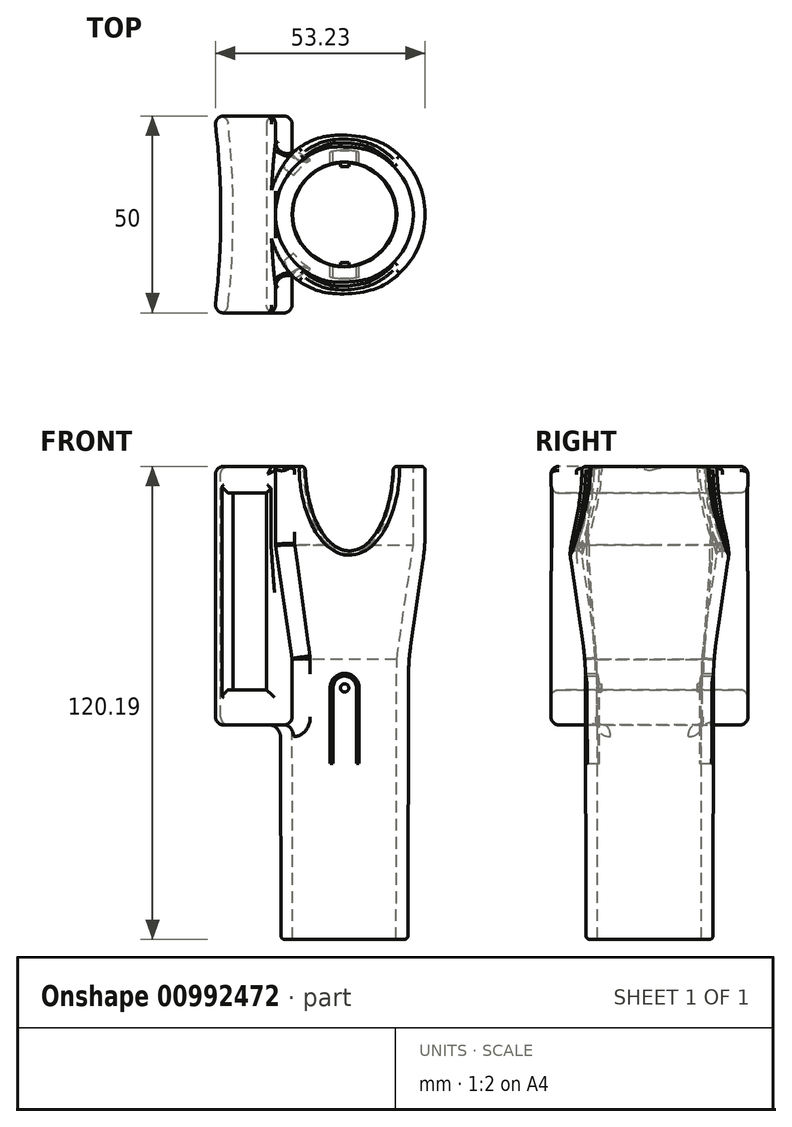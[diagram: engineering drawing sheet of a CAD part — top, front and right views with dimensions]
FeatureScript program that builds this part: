
annotation { "Feature Type Name" : "Feature", "Feature Type Description" : "" }
export const myFeature = defineFeature(function(context is Context, id is Id, definition is map)
    precondition{}
    {
        {
            var Q0;
            Q0=qCreatedBy(makeId("Front.planeOp"),FACE);
            var sketch = newSketch(context, id + "F0", { "sketchPlane" : qUnion([Q0])});
            skLineSegment(sketch, "E0", {"start": v(-0.06, 65.68) * mm, "end": v(-0.06, -68.18) * mm, "construction": true});
            skLineSegment(sketch, "E1", {"start": v(-17.56, 65.68) * mm, "end": v(-17.56, 45.68) * mm});
            skLineSegment(sketch, "E2", {"start": v(-17.56, 45.68) * mm, "end": v(-13.36, 16.68) * mm});
            skLineSegment(sketch, "E3", {"start": v(-13.36, 16.68) * mm, "end": v(-13.2, -54.45) * mm});
            skLineSegment(sketch, "E4.0", {"start": v(-16.36, 16.46) * mm, "end": v(-16.2, -54.54) * mm});
            skLineSegment(sketch, "E4.1", {"start": v(-20.56, 45.46) * mm, "end": v(-16.36, 16.46) * mm});
            skLineSegment(sketch, "E4.2", {"start": v(-20.56, 65.68) * mm, "end": v(-20.56, 45.46) * mm});
            skLineSegment(sketch, "E5", {"start": v(-20.56, 65.68) * mm, "end": v(-17.56, 65.68) * mm});
            skLineSegment(sketch, "E6", {"start": v(-16.2, -54.54) * mm, "end": v(-13.2, -54.45) * mm});
            skLineSegment(sketch, "E7", {"start": v(-20.56, 58.97) * mm, "end": v(-20.56, 45.46) * mm});
            skSolve(sketch);
        }
        {
            var Q0;
            Q0=makeQuery(id+"F0.imprint","IMPRINT",FACE,{"disambiguationData":[TD([[makeQuery(id+"F0.imprint","IMPRINT",EDGE,{"derivedFrom":sQuery(id+"F0.wireOp",EDGE,"E1")}),-1.0]])]});
            var Q1;
            Q1=sQuery(id+"F0.wireOp",EDGE,"E0");
            revolve(context, id + "F1", {"surfaceOperationType" : NewSurfaceOperationType.NEW, "entities" : qUnion([Q0]), "axis" : qUnion([Q1]), "revolveType" : RevolveType.FULL});
        }
        {
            var Q0;
            Q0=makeQuery(id+"F1.opRevolve","SWEPT_EDGE",EDGE,{"disambiguationData":[OSD([sQuery(id+"F0.wireOp",EDGE,"E4.2"),sQuery(id+"F0.wireOp",EDGE,"E5")])]});
            var Q1;
            Q1=makeQuery(id+"F1.opRevolve","SWEPT_EDGE",EDGE,{"disambiguationData":[OSD([sQuery(id+"F0.wireOp",EDGE,"E4.0"),sQuery(id+"F0.wireOp",EDGE,"E6")])]});
            var Q2;
            Q2=makeQuery(id+"F1.opRevolve","SWEPT_EDGE",EDGE,{"disambiguationData":[OSD([sQuery(id+"F0.wireOp",EDGE,"E1"),sQuery(id+"F0.wireOp",EDGE,"E5")])]});
            fillet(context, id + "F2", {"entities" : qUnion([Q0, Q1, Q2]), "radius" : 1 * mm, "tangentPropagation" : true, "allowEdgeOverflow" : false});
        }
        {
            var Q0;
            Q0=makeQuery(id+"F1.opRevolve","SWEPT_EDGE",EDGE,{"disambiguationData":[OSD([sQuery(id+"F0.wireOp",EDGE,"E4.1"),sQuery(id+"F0.wireOp",EDGE,"E7")])]});
            var Q1;
            Q1=makeQuery(id+"F1.opRevolve","SWEPT_EDGE",EDGE,{"disambiguationData":[OSD([sQuery(id+"F0.wireOp",EDGE,"E4.1"),sQuery(id+"F0.wireOp",EDGE,"WHEgpJMP-5o6V-psrv-Qzt2-RURnIkNBwz3v")])]});
            fillet(context, id + "F3", {"entities" : qUnion([Q0, Q1]), "radius" : 50 * mm, "tangentPropagation" : true, "allowEdgeOverflow" : false});
        }
        {
            var Q0;
            Q0=qCreatedBy(makeId("Front.planeOp"),FACE);
            var sketch = newSketch(context, id + "F4", { "sketchPlane" : qUnion([Q0])});
            skLineSegment(sketch, "E8", {"start": v(-17.56, 65.68) * mm, "end": v(-17.56, 45.68) * mm});
            skLineSegment(sketch, "E9", {"start": v(-13.36, 0) * mm, "end": v(-33.36, 0) * mm});
            skLineSegment(sketch, "E10", {"start": v(-33.36, 0) * mm, "end": v(-33.36, 65.68) * mm});
            skLineSegment(sketch, "E11", {"start": v(-33.36, 65.68) * mm, "end": v(-17.56, 65.68) * mm});
            skLineSegment(sketch, "E12", {"start": v(-13.36, 16.68) * mm, "end": v(-13.36, 0) * mm});
            skLineSegment(sketch, "E13", {"start": v(-17.56, 45.68) * mm, "end": v(-13.36, 16.68) * mm});
            skSolve(sketch);
        }
        {
            var Q0;
            Q0=makeQuery(id+"F4.imprint","IMPRINT",FACE,{"disambiguationData":[TD([[makeQuery(id+"F4.imprint","IMPRINT",EDGE,{"derivedFrom":sQuery(id+"F4.wireOp",EDGE,"E8")}),-1.0]])]});
            extrude(context, id + "F5", {"entities" : qUnion([Q0]), "operationType" : NewBodyOperationType.ADD, "endBound" : BoundingType.SYMMETRIC, "depth" : 50 * mm, "offsetDistance" : 25 * mm});
        }
        {
            var Q0;
            Q0=qCreatedBy(makeId("Front.planeOp"),FACE);
            var sketch = newSketch(context, id + "F6", { "sketchPlane" : qUnion([Q0])});
            skLineSegment(sketch, "E14", {"start": v(-24.08, 72.46) * mm, "end": v(-24.08, -4.6) * mm, "construction": true});
            skLineSegment(sketch, "E15.bottom", {"start": v(-19.83, 8.93) * mm, "end": v(-28.33, 8.93) * mm});
            skLineSegment(sketch, "E15.top", {"start": v(-19.83, 58.93) * mm, "end": v(-28.33, 58.93) * mm});
            skLineSegment(sketch, "E15.left", {"start": v(-19.83, 8.93) * mm, "end": v(-19.83, 58.93) * mm});
            skLineSegment(sketch, "E15.right", {"start": v(-28.33, 8.93) * mm, "end": v(-28.33, 58.93) * mm});
            skSolve(sketch);
        }
        {
            var Q0;
            Q0 = qSketchRegion(id + "F8", true);
            var Q1;
            Q1 = qSketchRegion(id + "F6", true);
            extrude(context, id + "F7", {"entities" : qUnion([Q0, Q1]), "operationType" : NewBodyOperationType.REMOVE, "endBound" : BoundingType.THROUGH_ALL, "oppositeDirection" : true, "depth" : 55 * mm, "offsetDistance" : 25 * mm, "hasSecondDirection" : true, "secondDirectionBound" : SecondDirectionBoundingType.THROUGH_ALL, "secondDirectionOppositeDirection" : false, "secondDirectionDepth" : 25 * mm});
        }
        {
            var Q0;
            Q0=makeQuery(id+"F5.opExtrude","SWEPT_FACE",FACE,{"disambiguationData":[OSD([sQuery(id+"F4.wireOp",EDGE,"E11")])]});
            var sketch = newSketch(context, id + "F8", { "sketchPlane" : qUnion([Q0])});
            skCircle(sketch, "E16", {"center": v(-235.26, 0) * mm, "radius": 211.06 * mm});
            skPoint(sketch, "E17", {"position": v(-33.36, 0) * mm});
            skSolve(sketch);
        }
        {
            var Q0;
            Q0 = qSketchRegion(id + "F6", true);
            var Q1;
            Q1=sQuery(id+"F8.wireOp",EDGE,"E16");
            sweep(context, id + "F9", {"operationType" : NewBodyOperationType.REMOVE, "profiles" : qUnion([Q0]), "path" : qUnion([Q1])});
        }
        {
            var Q0;
            {var subQ1=sQuery(id+"F4.wireOp",EDGE,"E11");var subQ6=makeQuery(id+"F5.opExtrude","SWEPT_EDGE",EDGE,{"disambiguationData":[OSD([sQuery(id+"F4.wireOp",EDGE,"E10"),subQ1])]});Q0=makeQuery(id+"F8.imprint","IMPRINT",FACE,{"disambiguationData":[TD([[makeQuery(id+"F8.imprint","IMPRINT",EDGE,{"derivedFrom":subQ6}),1.0]])]});}
            var sketch = newSketch(context, id + "F10", { "sketchPlane" : qUnion([Q0])});
            skCircle(sketch, "E18.0", {"center": v(-235.26, 0) * mm, "radius": 203.76 * mm});
            skSolve(sketch);
        }
        {
            var Q0;
            {var subQ1=sQuery(id+"F4.wireOp",EDGE,"E11");var subQ3=makeQuery(id+"F5.opExtrude","SWEPT_EDGE",EDGE,{"disambiguationData":[OSD([sQuery(id+"F4.wireOp",EDGE,"E10"),subQ1])]});var subQ10=makeQuery(id+"F8.imprint","IMPRINT",EDGE,{"derivedFrom":subQ3});Q0=makeQuery(id+"F10.imprint","IMPRINT",FACE,{"disambiguationData":[TD([[makeQuery(id+"F10.imprint","IMPRINT",EDGE,{"derivedFrom":subQ10}),-1.0]])]});}
            var Q1;
            Q1=sQuery(id+"F10.wireOp",EDGE,"E18.0");
            extrude(context, id + "F11", {"entities" : qUnion([Q0]), "operationType" : NewBodyOperationType.REMOVE, "surfaceEntities" : qUnion([Q1]), "endBound" : BoundingType.THROUGH_ALL, "oppositeDirection" : true, "depth" : 25 * mm, "offsetDistance" : 25 * mm});
        }
        {
            var Q0;
            Q0=makeQuery(id+"F11.boolean.opBoolean","COPY",EDGE,{"derivedFrom":makeQuery(id+"F11.opExtrude","CAP_EDGE",EDGE,{"disambiguationData":[OSD([sQuery(id+"F10.wireOp",EDGE,"E18.0")])],"isStart":true})});
            var Q1;
            Q1=makeQuery(id+"F5.opExtrude","CAP_EDGE",EDGE,{"disambiguationData":[OSD([sQuery(id+"F4.wireOp",EDGE,"E11")])],"isStart":false});
            var Q2;
            {var subQ0=sQuery(id+"F10.wireOp",EDGE,"E18.0");var subQ1=sQuery(id+"F4.wireOp",EDGE,"E11");var subQ2=makeQuery(id+"F5.opExtrude","CAP_EDGE",EDGE,{"disambiguationData":[OSD([subQ1])],"isStart":false});Q2=makeQuery(id+"F11.boolean.opBoolean","COPY",EDGE,{"derivedFrom":makeQuery(id+"F11.opExtrude","SWEPT_EDGE",EDGE,{"disambiguationData":[OSD([subQ1,subQ0]),TDD([makeQuery(id+"F10.imprint","INTERSECT",VERTEX,{"derivedFrom":[makeQuery(id+"F8.imprint","IMPRINT",EDGE,{"disambiguationData":[TD([[makeQuery(id+"F8.imprint","INTERSECT",VERTEX,{"derivedFrom":[subQ2,sQuery(id+"F8.wireOp",EDGE,"E16")]}),1.0]])],"derivedFrom":subQ2}),subQ0]})])]})});}
            var Q3;
            Q3=makeQuery(id+"F5.opExtrude","CAP_EDGE",EDGE,{"disambiguationData":[OSD([sQuery(id+"F4.wireOp",EDGE,"E9")])],"isStart":false});
            var Q4;
            {var subQ0=sQuery(id+"F10.wireOp",EDGE,"E18.0");var subQ1=sQuery(id+"F4.wireOp",EDGE,"E11");var subQ2=makeQuery(id+"F5.opExtrude","CAP_EDGE",EDGE,{"disambiguationData":[OSD([subQ1])],"isStart":true});Q4=makeQuery(id+"F11.boolean.opBoolean","COPY",EDGE,{"derivedFrom":makeQuery(id+"F11.opExtrude","SWEPT_EDGE",EDGE,{"disambiguationData":[OSD([subQ1,subQ0]),TDD([makeQuery(id+"F10.imprint","INTERSECT",VERTEX,{"derivedFrom":[makeQuery(id+"F8.imprint","IMPRINT",EDGE,{"disambiguationData":[TD([[makeQuery(id+"F8.imprint","INTERSECT",VERTEX,{"derivedFrom":[subQ2,sQuery(id+"F8.wireOp",EDGE,"E16")]}),1.0]])],"derivedFrom":subQ2}),subQ0]})])]})});}
            var Q5;
            Q5=makeQuery(id+"F11.boolean.opBoolean","INTERSECT",EDGE,{"derivedFrom":[makeQuery(id+"F5.opExtrude","SWEPT_FACE",FACE,{"disambiguationData":[OSD([sQuery(id+"F4.wireOp",EDGE,"E9")])]}),makeQuery(id+"F11.opExtrude","SWEPT_FACE",FACE,{"disambiguationData":[OSD([sQuery(id+"F10.wireOp",EDGE,"E18.0")])]})]});
            var Q6;
            {var subQ0=sQuery(id+"F4.wireOp",EDGE,"E9");var subQ1=sQuery(id+"F4.wireOp",EDGE,"E12");Q6=makeQuery(id+"F5.boolean.opBoolean","SPLIT",EDGE,{"disambiguationData":[TD([makeQuery(id+"F5.opExtrude","CAP_FACE",FACE,{"disambiguationData":[OSD([sQuery(id+"F4.wireOp",EDGE,"E8"),subQ0,sQuery(id+"F4.wireOp",EDGE,"E10"),sQuery(id+"F4.wireOp",EDGE,"E11"),subQ1,sQuery(id+"F4.wireOp",EDGE,"E13")])],"isStart":false})])],"derivedFrom":makeQuery(id+"F5.opExtrude","SWEPT_EDGE",EDGE,{"disambiguationData":[OSD([subQ0,subQ1])]})});}
            var Q7;
            {var subQ0=sQuery(id+"F4.wireOp",EDGE,"E9");var subQ1=sQuery(id+"F4.wireOp",EDGE,"E12");Q7=makeQuery(id+"F5.boolean.opBoolean","SPLIT",EDGE,{"disambiguationData":[TD([makeQuery(id+"F5.opExtrude","CAP_FACE",FACE,{"disambiguationData":[OSD([sQuery(id+"F4.wireOp",EDGE,"E8"),subQ0,sQuery(id+"F4.wireOp",EDGE,"E10"),sQuery(id+"F4.wireOp",EDGE,"E11"),subQ1,sQuery(id+"F4.wireOp",EDGE,"E13")])],"isStart":true})])],"derivedFrom":makeQuery(id+"F5.opExtrude","SWEPT_EDGE",EDGE,{"disambiguationData":[OSD([subQ0,subQ1])]})});}
            var Q8;
            Q8=makeQuery(id+"F5.opExtrude","CAP_EDGE",EDGE,{"disambiguationData":[OSD([sQuery(id+"F4.wireOp",EDGE,"E11")])],"isStart":true});
            var Q9;
            Q9=makeQuery(id+"F5.opExtrude","CAP_EDGE",EDGE,{"disambiguationData":[OSD([sQuery(id+"F4.wireOp",EDGE,"E12")])],"isStart":false});
            var Q10;
            Q10=makeQuery(id+"F5.opExtrude","CAP_EDGE",EDGE,{"disambiguationData":[OSD([sQuery(id+"F4.wireOp",EDGE,"E13")])],"isStart":false});
            var Q11;
            Q11=makeQuery(id+"F5.opExtrude","CAP_EDGE",EDGE,{"disambiguationData":[OSD([sQuery(id+"F4.wireOp",EDGE,"E8")])],"isStart":false});
            var Q12;
            Q12=makeQuery(id+"F5.opExtrude","CAP_EDGE",EDGE,{"disambiguationData":[OSD([sQuery(id+"F4.wireOp",EDGE,"E12")])],"isStart":true});
            var Q13;
            Q13=makeQuery(id+"F5.opExtrude","CAP_EDGE",EDGE,{"disambiguationData":[OSD([sQuery(id+"F4.wireOp",EDGE,"E13")])],"isStart":true});
            var Q14;
            Q14=makeQuery(id+"F5.opExtrude","CAP_EDGE",EDGE,{"disambiguationData":[OSD([sQuery(id+"F4.wireOp",EDGE,"E8")])],"isStart":true});
            var Q15;
            {var subQ0=sQuery(id+"F4.wireOp",EDGE,"E13");var subQ1=sQuery(id+"F4.wireOp",EDGE,"E12");Q15=makeQuery(id+"F5.boolean.opBoolean","SPLIT",EDGE,{"disambiguationData":[TD([makeQuery(id+"F5.opExtrude","CAP_FACE",FACE,{"disambiguationData":[OSD([sQuery(id+"F4.wireOp",EDGE,"E8"),sQuery(id+"F4.wireOp",EDGE,"E9"),sQuery(id+"F4.wireOp",EDGE,"E10"),sQuery(id+"F4.wireOp",EDGE,"E11"),subQ1,subQ0])],"isStart":true})])],"derivedFrom":makeQuery(id+"F5.opExtrude","SWEPT_EDGE",EDGE,{"disambiguationData":[OSD([subQ1,subQ0])]})});}
            var Q16;
            {var subQ0=sQuery(id+"F4.wireOp",EDGE,"E13");var subQ1=sQuery(id+"F4.wireOp",EDGE,"E8");Q16=makeQuery(id+"F5.boolean.opBoolean","SPLIT",EDGE,{"disambiguationData":[TD([makeQuery(id+"F5.opExtrude","CAP_FACE",FACE,{"disambiguationData":[OSD([subQ1,sQuery(id+"F4.wireOp",EDGE,"E9"),sQuery(id+"F4.wireOp",EDGE,"E10"),sQuery(id+"F4.wireOp",EDGE,"E11"),sQuery(id+"F4.wireOp",EDGE,"E12"),subQ0])],"isStart":true})])],"derivedFrom":makeQuery(id+"F5.opExtrude","SWEPT_EDGE",EDGE,{"disambiguationData":[OSD([subQ1,subQ0])]})});}
            var Q17;
            {var subQ0=sQuery(id+"F4.wireOp",EDGE,"E13");var subQ1=sQuery(id+"F4.wireOp",EDGE,"E12");Q17=makeQuery(id+"F5.boolean.opBoolean","SPLIT",EDGE,{"disambiguationData":[TD([makeQuery(id+"F5.opExtrude","CAP_FACE",FACE,{"disambiguationData":[OSD([sQuery(id+"F4.wireOp",EDGE,"E8"),sQuery(id+"F4.wireOp",EDGE,"E9"),sQuery(id+"F4.wireOp",EDGE,"E10"),sQuery(id+"F4.wireOp",EDGE,"E11"),subQ1,subQ0])],"isStart":false})])],"derivedFrom":makeQuery(id+"F5.opExtrude","SWEPT_EDGE",EDGE,{"disambiguationData":[OSD([subQ1,subQ0])]})});}
            var Q18;
            {var subQ0=sQuery(id+"F4.wireOp",EDGE,"E13");var subQ1=sQuery(id+"F4.wireOp",EDGE,"E8");Q18=makeQuery(id+"F5.boolean.opBoolean","SPLIT",EDGE,{"disambiguationData":[TD([makeQuery(id+"F5.opExtrude","CAP_FACE",FACE,{"disambiguationData":[OSD([subQ1,sQuery(id+"F4.wireOp",EDGE,"E9"),sQuery(id+"F4.wireOp",EDGE,"E10"),sQuery(id+"F4.wireOp",EDGE,"E11"),sQuery(id+"F4.wireOp",EDGE,"E12"),subQ0])],"isStart":false})])],"derivedFrom":makeQuery(id+"F5.opExtrude","SWEPT_EDGE",EDGE,{"disambiguationData":[OSD([subQ1,subQ0])]})});}
            fillet(context, id + "F12", {"entities" : qUnion([Q0, Q1, Q2, Q3, Q4, Q5, Q6, Q7, Q8, Q9, Q10, Q11, Q12, Q13, Q14, Q15, Q16, Q17, Q18]), "radius" : 2 * mm, "tangentPropagation" : true, "allowEdgeOverflow" : false});
        }
        {
            var Q0;
            Q0=makeQuery(id+"F9.boolean.opBoolean","INTERSECT",EDGE,{"derivedFrom":[makeQuery(id+"F5.opExtrude","CAP_FACE",FACE,{"disambiguationData":[OSD([sQuery(id+"F4.wireOp",EDGE,"E8"),sQuery(id+"F4.wireOp",EDGE,"E9"),sQuery(id+"F4.wireOp",EDGE,"E10"),sQuery(id+"F4.wireOp",EDGE,"E11"),sQuery(id+"F4.wireOp",EDGE,"E12"),sQuery(id+"F4.wireOp",EDGE,"E13")])],"isStart":false}),makeQuery(id+"F9.opSweep","SWEPT_FACE",FACE,{"disambiguationData":[OSD([sQuery(id+"F6.wireOp",EDGE,"E15.right"),sQuery(id+"F8.wireOp",EDGE,"E16")])]})]});
            var Q1;
            Q1=makeQuery(id+"F9.boolean.opBoolean","INTERSECT",EDGE,{"derivedFrom":[makeQuery(id+"F5.opExtrude","CAP_FACE",FACE,{"disambiguationData":[OSD([sQuery(id+"F4.wireOp",EDGE,"E8"),sQuery(id+"F4.wireOp",EDGE,"E9"),sQuery(id+"F4.wireOp",EDGE,"E10"),sQuery(id+"F4.wireOp",EDGE,"E11"),sQuery(id+"F4.wireOp",EDGE,"E12"),sQuery(id+"F4.wireOp",EDGE,"E13")])],"isStart":false}),makeQuery(id+"F9.opSweep","SWEPT_FACE",FACE,{"disambiguationData":[OSD([sQuery(id+"F6.wireOp",EDGE,"E15.top"),sQuery(id+"F8.wireOp",EDGE,"E16")])]})]});
            var Q2;
            Q2=makeQuery(id+"F9.boolean.opBoolean","INTERSECT",EDGE,{"derivedFrom":[makeQuery(id+"F5.opExtrude","CAP_FACE",FACE,{"disambiguationData":[OSD([sQuery(id+"F4.wireOp",EDGE,"E8"),sQuery(id+"F4.wireOp",EDGE,"E9"),sQuery(id+"F4.wireOp",EDGE,"E10"),sQuery(id+"F4.wireOp",EDGE,"E11"),sQuery(id+"F4.wireOp",EDGE,"E12"),sQuery(id+"F4.wireOp",EDGE,"E13")])],"isStart":true}),makeQuery(id+"F9.opSweep","SWEPT_FACE",FACE,{"disambiguationData":[OSD([sQuery(id+"F6.wireOp",EDGE,"E15.right"),sQuery(id+"F8.wireOp",EDGE,"E16")])]})]});
            var Q3;
            Q3=makeQuery(id+"F9.boolean.opBoolean","INTERSECT",EDGE,{"derivedFrom":[makeQuery(id+"F5.opExtrude","CAP_FACE",FACE,{"disambiguationData":[OSD([sQuery(id+"F4.wireOp",EDGE,"E8"),sQuery(id+"F4.wireOp",EDGE,"E9"),sQuery(id+"F4.wireOp",EDGE,"E10"),sQuery(id+"F4.wireOp",EDGE,"E11"),sQuery(id+"F4.wireOp",EDGE,"E12"),sQuery(id+"F4.wireOp",EDGE,"E13")])],"isStart":true}),makeQuery(id+"F9.opSweep","SWEPT_FACE",FACE,{"disambiguationData":[OSD([sQuery(id+"F6.wireOp",EDGE,"E15.top"),sQuery(id+"F8.wireOp",EDGE,"E16")])]})]});
            fillet(context, id + "F13", {"entities" : qUnion([Q0, Q1, Q2, Q3]), "radius" : 2 * mm, "tangentPropagation" : true, "allowEdgeOverflow" : false});
        }
        {
            var Q0;
            Q0=makeQuery(id+"F7.boolean.opBoolean","INTERSECT",EDGE,{"derivedFrom":[makeQuery(id+"F5.opExtrude","CAP_FACE",FACE,{"disambiguationData":[OSD([sQuery(id+"F4.wireOp",EDGE,"E8"),sQuery(id+"F4.wireOp",EDGE,"E9"),sQuery(id+"F4.wireOp",EDGE,"E10"),sQuery(id+"F4.wireOp",EDGE,"E11"),sQuery(id+"F4.wireOp",EDGE,"E12"),sQuery(id+"F4.wireOp",EDGE,"E13")])],"isStart":false}),makeQuery(id+"F7.opExtrude","SWEPT_FACE",FACE,{"disambiguationData":[OSD([sQuery(id+"F6.wireOp",EDGE,"E15.left")])]})]});
            var Q1;
            Q1=makeQuery(id+"F9.boolean.opBoolean","INTERSECT",EDGE,{"derivedFrom":[makeQuery(id+"F5.opExtrude","CAP_FACE",FACE,{"disambiguationData":[OSD([sQuery(id+"F4.wireOp",EDGE,"E8"),sQuery(id+"F4.wireOp",EDGE,"E9"),sQuery(id+"F4.wireOp",EDGE,"E10"),sQuery(id+"F4.wireOp",EDGE,"E11"),sQuery(id+"F4.wireOp",EDGE,"E12"),sQuery(id+"F4.wireOp",EDGE,"E13")])],"isStart":false}),makeQuery(id+"F9.opSweep","SWEPT_FACE",FACE,{"disambiguationData":[OSD([sQuery(id+"F6.wireOp",EDGE,"E15.bottom"),sQuery(id+"F8.wireOp",EDGE,"E16")])]})]});
            var Q2;
            Q2=makeQuery(id+"F7.boolean.opBoolean","INTERSECT",EDGE,{"derivedFrom":[makeQuery(id+"F5.opExtrude","CAP_FACE",FACE,{"disambiguationData":[OSD([sQuery(id+"F4.wireOp",EDGE,"E8"),sQuery(id+"F4.wireOp",EDGE,"E9"),sQuery(id+"F4.wireOp",EDGE,"E10"),sQuery(id+"F4.wireOp",EDGE,"E11"),sQuery(id+"F4.wireOp",EDGE,"E12"),sQuery(id+"F4.wireOp",EDGE,"E13")])],"isStart":true}),makeQuery(id+"F7.opExtrude","SWEPT_FACE",FACE,{"disambiguationData":[OSD([sQuery(id+"F6.wireOp",EDGE,"E15.left")])]})]});
            var Q3;
            Q3=makeQuery(id+"F9.boolean.opBoolean","INTERSECT",EDGE,{"derivedFrom":[makeQuery(id+"F5.opExtrude","CAP_FACE",FACE,{"disambiguationData":[OSD([sQuery(id+"F4.wireOp",EDGE,"E8"),sQuery(id+"F4.wireOp",EDGE,"E9"),sQuery(id+"F4.wireOp",EDGE,"E10"),sQuery(id+"F4.wireOp",EDGE,"E11"),sQuery(id+"F4.wireOp",EDGE,"E12"),sQuery(id+"F4.wireOp",EDGE,"E13")])],"isStart":true}),makeQuery(id+"F9.opSweep","SWEPT_FACE",FACE,{"disambiguationData":[OSD([sQuery(id+"F6.wireOp",EDGE,"E15.bottom"),sQuery(id+"F8.wireOp",EDGE,"E16")])]})]});
            fillet(context, id + "F14", {"entities" : qUnion([Q0, Q1, Q2, Q3]), "radius" : 2 * mm, "tangentPropagation" : true, "allowEdgeOverflow" : false});
        }
        {
            var Q0;
            {var subQ0=sQuery(id+"F4.wireOp",EDGE,"E11");var subQ1=sQuery(id+"F4.wireOp",EDGE,"E8");Q0=makeQuery(id+"F5.boolean.opBoolean","SPLIT",EDGE,{"disambiguationData":[TD([makeQuery(id+"F5.opExtrude","CAP_FACE",FACE,{"disambiguationData":[OSD([subQ1,sQuery(id+"F4.wireOp",EDGE,"E9"),sQuery(id+"F4.wireOp",EDGE,"E10"),subQ0,sQuery(id+"F4.wireOp",EDGE,"E12"),sQuery(id+"F4.wireOp",EDGE,"E13")])],"isStart":true})])],"derivedFrom":makeQuery(id+"F5.opExtrude","SWEPT_EDGE",EDGE,{"disambiguationData":[OSD([subQ1,subQ0])]})});}
            var Q1;
            {var subQ0=sQuery(id+"F4.wireOp",EDGE,"E11");var subQ1=sQuery(id+"F4.wireOp",EDGE,"E8");Q1=makeQuery(id+"F5.boolean.opBoolean","SPLIT",EDGE,{"disambiguationData":[TD([makeQuery(id+"F5.opExtrude","CAP_FACE",FACE,{"disambiguationData":[OSD([subQ1,sQuery(id+"F4.wireOp",EDGE,"E9"),sQuery(id+"F4.wireOp",EDGE,"E10"),subQ0,sQuery(id+"F4.wireOp",EDGE,"E12"),sQuery(id+"F4.wireOp",EDGE,"E13")])],"isStart":false})])],"derivedFrom":makeQuery(id+"F5.opExtrude","SWEPT_EDGE",EDGE,{"disambiguationData":[OSD([subQ1,subQ0])]})});}
            fillet(context, id + "F15", {"entities" : qUnion([Q0, Q1]), "radius" : 1 * mm, "tangentPropagation" : true, "allowEdgeOverflow" : false});
        }
        {
            var Q0;
            Q0=qCreatedBy(makeId("Front.planeOp"),FACE);
            var sketch = newSketch(context, id + "F16", { "sketchPlane" : qUnion([Q0])});
            skLineSegment(sketch, "E19", {"start": v(-21.9, -64.41) * mm, "end": v(45.25, -64.41) * mm, "construction": true});
            skCircle(sketch, "E20", {"center": v(0, 9.39) * mm, "radius": 1 * mm});
            skArc(sketch, "E21", {"start": v(3, 9.39) * mm, "mid": v(0, 12.39) * mm, "end": v(-3, 9.39) * mm});
            skLineSegment(sketch, "E22.left", {"start": v(-3, 9.39) * mm, "end": v(-3, -9.85) * mm});
            skLineSegment(sketch, "E22.right", {"start": v(3, 9.39) * mm, "end": v(3, -9.85) * mm});
            skLineSegment(sketch, "E23.0", {"start": v(-3.7, 9.39) * mm, "end": v(-3.7, -9.85) * mm});
            skArc(sketch, "E23.1", {"start": v(3.7, 9.39) * mm, "mid": v(0, 13.09) * mm, "end": v(-3.7, 9.39) * mm});
            skLineSegment(sketch, "E23.2", {"start": v(3.7, 9.39) * mm, "end": v(3.7, -9.85) * mm});
            skLineSegment(sketch, "E24", {"start": v(-3.7, -9.85) * mm, "end": v(-3, -9.85) * mm});
            skLineSegment(sketch, "E25", {"start": v(3, -9.85) * mm, "end": v(3.7, -9.85) * mm});
            skSolve(sketch);
        }
        {
            var Q0;
            Q0 = qSketchRegion(id + "F16", true);
            extrude(context, id + "F17", {"entities" : qUnion([Q0]), "operationType" : NewBodyOperationType.REMOVE, "endBound" : BoundingType.THROUGH_ALL, "depth" : 25 * mm, "offsetDistance" : 25 * mm, "hasSecondDirection" : true, "secondDirectionOppositeDirection" : true, "secondDirectionDepth" : 25 * mm});
        }
        {
            var Q0;
            Q0=qCreatedBy(makeId("Front.planeOp"),FACE);
            var sketch = newSketch(context, id + "F18", { "sketchPlane" : qUnion([Q0])});
            skCircle(sketch, "E26", {"center": v(0, 9.4) * mm, "radius": 1.05 * mm});
            skSolve(sketch);
        }
        {
            var Q0;
            Q0 = qSketchRegion(id + "F18", true);
            extrude(context, id + "F19", {"entities" : qUnion([Q0]), "operationType" : NewBodyOperationType.ADD, "depth" : 16.3 * mm, "offsetDistance" : 25 * mm, "hasSecondDirection" : true, "secondDirectionOppositeDirection" : false, "secondDirectionDepth" : 12.2 * mm});
        }
        {
            var Q0;
            {var subQ0=sQuery(id+"F4.wireOp",EDGE,"E8");var subQ2=sQuery(id+"F4.wireOp",EDGE,"E12");var subQ3=sQuery(id+"F4.wireOp",EDGE,"E13");Q0=makeQuery(id+"F5.boolean.opBoolean","SPLIT",FACE,{"disambiguationData":[TD([makeQuery(id+"F5.opExtrude","CAP_FACE",FACE,{"disambiguationData":[OSD([subQ0,sQuery(id+"F4.wireOp",EDGE,"E9"),sQuery(id+"F4.wireOp",EDGE,"E10"),sQuery(id+"F4.wireOp",EDGE,"E11"),subQ2,subQ3])],"isStart":false})])],"derivedFrom":makeQuery(id+"F5.opExtrude","SWEPT_FACE",FACE,{"disambiguationData":[OSD([subQ3])]})});}
            fillet(context, id + "F20", {"entities" : qUnion([Q0]), "radius" : 3 * mm, "tangentPropagation" : true, "allowEdgeOverflow" : false});
        }
        {
            var Q0;
            Q0 = qSketchRegion(id + "F18", true);
            extrude(context, id + "F21", {"entities" : qUnion([Q0]), "operationType" : NewBodyOperationType.ADD, "depth" : -16.3 * mm, "offsetDistance" : 25 * mm, "hasSecondDirection" : true, "secondDirectionOppositeDirection" : false, "secondDirectionDepth" : -12.2 * mm});
        }
        {
            var Q0;
            Q0=makeQuery(id+"F5.opExtrude","CAP_EDGE",EDGE,{"disambiguationData":[OSD([sQuery(id+"F4.wireOp",EDGE,"E9")])],"isStart":true});
            fillet(context, id + "F22", {"entities" : qUnion([Q0]), "radius" : 2 * mm, "tangentPropagation" : true, "allowEdgeOverflow" : false});
        }
        {
            var Q0;
            Q0=qCreatedBy(makeId("Front.planeOp"),FACE);
            var sketch = newSketch(context, id + "F23", { "sketchPlane" : qUnion([Q0])});
            skEllipse(sketch, "E27", {"center": v(1.16, 66.16) * mm, "majorRadius": 21.94 * mm, "minorRadius": 11.17 * mm, "majorAxis": v(0, -1)});
            skSolve(sketch);
        }
        {
            var Q0;
            Q0=makeQuery(id+"F23.imprint","IMPRINT",FACE,{"disambiguationData":[TD([[makeQuery(id+"F23.imprint","IMPRINT",EDGE,{"derivedFrom":sQuery(id+"F23.wireOp",EDGE,"E27")}),1.0]])]});
            extrude(context, id + "F24", {"entities" : qUnion([Q0]), "operationType" : NewBodyOperationType.REMOVE, "depth" : 25 * mm, "offsetDistance" : 25 * mm, "hasSecondDirection" : true, "secondDirectionOppositeDirection" : true, "secondDirectionDepth" : 25 * mm});
        }
        {
            var Q0;
            Q0=makeQuery(id+"F24.boolean.opBoolean","COPY",FACE,{"disambiguationData":[OD(1.0)],"derivedFrom":makeQuery(id+"F24.opExtrude","SWEPT_FACE",FACE,{"disambiguationData":[OSD([sQuery(id+"F23.wireOp",EDGE,"xSoHhAKU-rOEn-gmhi-UZDl-cR2wID1O0WQS")])]})});
            var Q1;
            Q1=makeQuery(id+"F24.boolean.opBoolean","COPY",FACE,{"disambiguationData":[OD(0.0)],"derivedFrom":makeQuery(id+"F24.opExtrude","SWEPT_FACE",FACE,{"disambiguationData":[OSD([sQuery(id+"F23.wireOp",EDGE,"xSoHhAKU-rOEn-gmhi-UZDl-cR2wID1O0WQS")])]})});
            var Q2;
            Q2=makeQuery(id+"F24.boolean.opBoolean","COPY",FACE,{"disambiguationData":[OD(1.0)],"derivedFrom":makeQuery(id+"F24.opExtrude","SWEPT_FACE",FACE,{"disambiguationData":[OSD([sQuery(id+"F23.wireOp",EDGE,"E27")])]})});
            var Q3;
            Q3=makeQuery(id+"F24.boolean.opBoolean","COPY",FACE,{"disambiguationData":[OD(0.0)],"derivedFrom":makeQuery(id+"F24.opExtrude","SWEPT_FACE",FACE,{"disambiguationData":[OSD([sQuery(id+"F23.wireOp",EDGE,"E27")])]})});
            fillet(context, id + "F25", {"entities" : qUnion([Q0, Q1, Q2, Q3]), "radius" : 1 * mm, "tangentPropagation" : true, "allowEdgeOverflow" : false});
        }
    });
